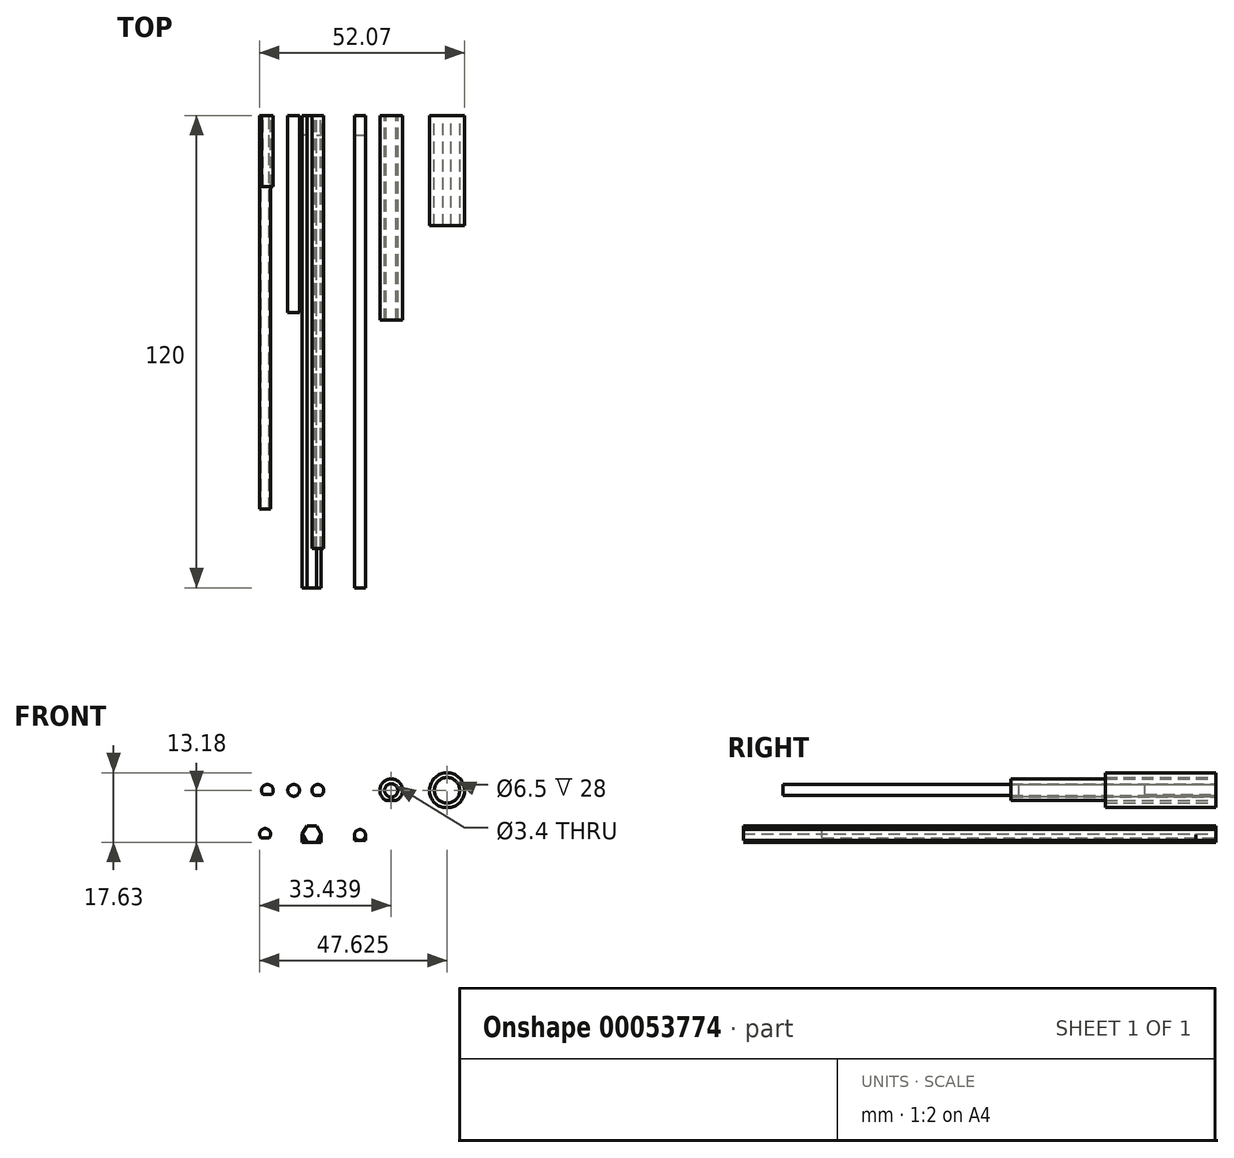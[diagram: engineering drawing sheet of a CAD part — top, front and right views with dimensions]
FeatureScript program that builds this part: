
annotation { "Feature Type Name" : "Feature", "Feature Type Description" : "" }
export const myFeature = defineFeature(function(context is Context, id is Id, definition is map)
    precondition{}
    {
        {
            var Q0;
            Q0=qCreatedBy(makeId("Front.planeOp"),FACE);
            var sketch = newSketch(context, id + "F0", { "sketchPlane" : qUnion([Q0])});
            skLineSegment(sketch, "E0", {"start": v(-14.5, 0) * mm, "end": v(47.28, 0) * mm, "construction": true});
            skLineSegment(sketch, "E1", {"start": v(-9.7, 3.28) * mm, "end": v(-9.7, -4.44) * mm, "construction": true});
            skCircle(sketch, "E2", {"center": v(-9.7, 0) * mm, "radius": 1.5 * mm});
            skPoint(sketch, "E3", {"position": v(-9.7, -1) * mm});
            skLineSegment(sketch, "E4", {"start": v(-10.82, -1) * mm, "end": v(-8.59, -1) * mm});
            skCircle(sketch, "E5", {"center": v(-3.04, 0) * mm, "radius": 1.5 * mm});
            skPoint(sketch, "E6", {"position": v(3.1, -1.3) * mm});
            skLineSegment(sketch, "E7", {"start": v(2.35, -1.3) * mm, "end": v(3.85, -1.3) * mm});
            skCircle(sketch, "E8", {"center": v(3.1, 0) * mm, "radius": 1.5 * mm});
            skLineSegment(sketch, "E9", {"start": v(7.92, -1.3) * mm, "end": v(9.42, -1.3) * mm});
            skCircle(sketch, "E10", {"center": v(8.67, 0) * mm, "radius": 1.5 * mm});
            skPoint(sketch, "E11", {"position": v(8.67, -1.3) * mm});
            skCircle(sketch, "E12", {"center": v(14.08, 0) * mm, "radius": 1.5 * mm});
            skLineSegment(sketch, "E13", {"start": v(13.33, -1.3) * mm, "end": v(14.83, -1.3) * mm});
            skPoint(sketch, "E14", {"position": v(14.08, -1.3) * mm});
            skCircle(sketch, "E15", {"center": v(21.75, 0) * mm, "radius": 1.7 * mm});
            skCircle(sketch, "E16", {"center": v(21.75, 0) * mm, "radius": 2.9 * mm});
            skLineSegment(sketch, "E17", {"start": v(21.75, 2.9) * mm, "end": v(21.75, -2.6) * mm, "construction": true});
            skLineSegment(sketch, "E18", {"start": v(20.46, -2.6) * mm, "end": v(23.03, -2.6) * mm});
            skCircle(sketch, "E19", {"center": v(-10.29, -11.1) * mm, "radius": 1.4 * mm});
            skLineSegment(sketch, "E20", {"start": v(-10.29, -7.78) * mm, "end": v(-10.29, -15.49) * mm, "construction": true});
            skLineSegment(sketch, "E21", {"start": v(-15.07, -11.1) * mm, "end": v(46.74, -11.1) * mm, "construction": true});
            skPoint(sketch, "E22", {"position": v(-10.29, -12.04) * mm});
            skLineSegment(sketch, "E23", {"start": v(-11.33, -12.04) * mm, "end": v(-9.25, -12.04) * mm});
            skCircle(sketch, "E24", {"center": v(35.93, 0) * mm, "radius": 4.45 * mm});
            skLineSegment(sketch, "E25", {"start": v(36.93, -4.34) * mm, "end": v(34.93, -4.34) * mm});
            skCircle(sketch, "E26", {"center": v(35.93, 0) * mm, "radius": 3.25 * mm});
            skCircle(sketch, "E27", {"center": v(1.53, -11.1) * mm, "radius": 2.4 * mm});
            skLineSegment(sketch, "E28.bottom", {"start": v(-0.87, -8.7) * mm, "end": v(3.93, -8.7) * mm});
            skLineSegment(sketch, "E28.top", {"start": v(-0.87, -13.18) * mm, "end": v(3.93, -13.18) * mm});
            skLineSegment(sketch, "E28.left", {"start": v(-0.87, -8.7) * mm, "end": v(-0.87, -13.18) * mm});
            skLineSegment(sketch, "E28.right", {"start": v(3.93, -8.7) * mm, "end": v(3.93, -13.18) * mm});
            skLineSegment(sketch, "E29", {"start": v(1.53, -8.7) * mm, "end": v(1.53, -13.5) * mm, "construction": true});
            skLineSegment(sketch, "E30.right", {"start": v(15.22, -9.95) * mm, "end": v(15.22, -12.75) * mm});
            skLineSegment(sketch, "E30.top", {"start": v(12.42, -12.75) * mm, "end": v(15.22, -12.75) * mm});
            skPoint(sketch, "E31", {"position": v(13.82, -11.35) * mm});
            skLineSegment(sketch, "E32", {"start": v(13.82, -9.95) * mm, "end": v(13.82, -12.75) * mm, "construction": true});
            skLineSegment(sketch, "E30.left", {"start": v(12.42, -9.95) * mm, "end": v(12.42, -12.75) * mm});
            skLineSegment(sketch, "E30.bottom", {"start": v(12.42, -9.95) * mm, "end": v(15.22, -9.95) * mm});
            skCircle(sketch, "E33", {"center": v(13.82, -11.35) * mm, "radius": 1.4 * mm});
            skPoint(sketch, "E34", {"position": v(0.33, -13.18) * mm});
            skPoint(sketch, "E35", {"position": v(2.73, -13.18) * mm});
            skCircle(sketch, "E36.cCircle", {"center": v(1.53, -11.1) * mm, "radius": 2.4 * mm, "construction": true});
            skLineSegment(sketch, "E36.0", {"start": v(-0.87, -11.1) * mm, "end": v(0.33, -9.03) * mm});
            skLineSegment(sketch, "E36.1", {"start": v(0.33, -9.03) * mm, "end": v(2.73, -9.03) * mm});
            skLineSegment(sketch, "E36.2", {"start": v(2.73, -9.03) * mm, "end": v(3.93, -11.1) * mm});
            skLineSegment(sketch, "E36.3", {"start": v(3.93, -11.1) * mm, "end": v(2.73, -13.18) * mm});
            skLineSegment(sketch, "E36.4", {"start": v(2.73, -13.18) * mm, "end": v(0.33, -13.18) * mm, "construction": true});
            skLineSegment(sketch, "E36.5", {"start": v(0.33, -13.18) * mm, "end": v(-0.87, -11.1) * mm});
            skSolve(sketch);
        }
        {
            var Q0;
            {var subQ0=sQuery(id+"F0.wireOp",EDGE,"E4");Q0=makeQuery(id+"F0.imprint","IMPRINT",FACE,{"disambiguationData":[TD([[makeQuery(id+"F0.imprint","IMPRINT",EDGE,{"derivedFrom":subQ0}),1.0]])]});}
            extrude(context, id + "F1", {"entities" : qUnion([Q0]), "depth" : 18 * mm});
        }
        {
            var Q0;
            Q0=makeQuery(id+"F0.imprint","IMPRINT",FACE,{"disambiguationData":[TD([[makeQuery(id+"F0.imprint","IMPRINT",EDGE,{"derivedFrom":sQuery(id+"F0.wireOp",EDGE,"E5")}),1.0]])]});
            extrude(context, id + "F2", {"entities" : qUnion([Q0]), "depth" : 50 * mm});
        }
        {
            var Q0;
            {var subQ0=sQuery(id+"F0.wireOp",EDGE,"E7");Q0=makeQuery(id+"F0.imprint","IMPRINT",FACE,{"disambiguationData":[TD([[makeQuery(id+"F0.imprint","IMPRINT",EDGE,{"derivedFrom":subQ0}),1.0]])]});}
            extrude(context, id + "F3", {"entities" : qUnion([Q0]), "depth" : 110 * mm});
        }
        {
            var Q0;
            {var subQ0=sQuery(id+"F0.wireOp",EDGE,"E23");Q0=makeQuery(id+"F0.imprint","IMPRINT",FACE,{"disambiguationData":[TD([[makeQuery(id+"F0.imprint","IMPRINT",EDGE,{"derivedFrom":subQ0}),1.0]])]});}
            extrude(context, id + "F4", {"entities" : qUnion([Q0]), "depth" : 100 * mm});
        }
        {
            var Q0;
            Q0=makeQuery(id+"F0.imprint","IMPRINT",FACE,{"disambiguationData":[TD([[makeQuery(id+"F0.imprint","IMPRINT",EDGE,{"derivedFrom":sQuery(id+"F0.wireOp",EDGE,"E15")}),-1.0]])]});
            extrude(context, id + "F5", {"entities" : qUnion([Q0]), "depth" : 52 * mm});
        }
        {
            var Q0;
            {var subQ0=sQuery(id+"F0.wireOp",EDGE,"E25");Q0=makeQuery(id+"F0.imprint","IMPRINT",FACE,{"disambiguationData":[TD([[makeQuery(id+"F0.imprint","IMPRINT",EDGE,{"derivedFrom":subQ0}),-1.0]])]});}
            extrude(context, id + "F6", {"entities" : qUnion([Q0]), "depth" : 28 * mm});
        }
        {
            var Q0;
            {var subQ0=sQuery(id+"F0.wireOp",EDGE,"E33");var subQ1=makeQuery(id+"F0.imprint","INTERSECT",VERTEX,{"derivedFrom":[sQuery(id+"F0.wireOp",EDGE,"E30.right"),subQ0]});Q0=makeQuery(id+"F0.imprint","IMPRINT",FACE,{"disambiguationData":[TD([[makeQuery(id+"F0.imprint","IMPRINT",EDGE,{"disambiguationData":[TD([[subQ1,-1.0]])],"derivedFrom":subQ0}),1.0]])]});}
            var Q1;
            {var subQ8=sQuery(id+"F0.wireOp",EDGE,"lmH1Ua7P-KBpo-EfuF-X9Tn-RCg2e1WFrg9c");Q1=makeQuery(id+"F0.imprint","IMPRINT",FACE,{"disambiguationData":[TD([[makeQuery(id+"F0.imprint","IMPRINT",EDGE,{"derivedFrom":subQ8}),1.0]])]});}
            var Q2;
            {var subQ0=sQuery(id+"F0.wireOp",EDGE,"sBpI47wx-J8by-lzRm-E1bE-YKL0DZhtYNUZ");Q2=makeQuery(id+"F0.imprint","IMPRINT",FACE,{"disambiguationData":[TD([[makeQuery(id+"F0.imprint","IMPRINT",EDGE,{"derivedFrom":subQ0}),-1.0]])]});}
            var Q3;
            {var subQ0=sQuery(id+"F0.wireOp",EDGE,"EQxFuaE4-UZCI-AMaP-Qjwn-iMiJtvs3Voor");Q3=makeQuery(id+"F0.imprint","IMPRINT",FACE,{"disambiguationData":[TD([[makeQuery(id+"F0.imprint","IMPRINT",EDGE,{"derivedFrom":subQ0}),1.0]])]});}
            var Q4;
            Q4=makeQuery(id+"F0.imprint","IMPRINT",FACE,{"disambiguationData":[TD([[makeQuery(id+"F0.imprint","IMPRINT",EDGE,{"derivedFrom":sQuery(id+"F0.wireOp",EDGE,"E36.0")}),-1.0]])]});
            extrude(context, id + "F7", {"entities" : qUnion([Q0, Q1, Q2, Q3, Q4]), "depth" : 120 * mm});
        }
        {
            var Q0;
            {var subQ0=sQuery(id+"F0.wireOp",EDGE,"EQxFuaE4-UZCI-AMaP-Qjwn-iMiJtvs3Voor");Q0=makeQuery(id+"F0.imprint","IMPRINT",FACE,{"disambiguationData":[TD([[makeQuery(id+"F0.imprint","IMPRINT",EDGE,{"derivedFrom":subQ0}),1.0]])]});}
            var Q1;
            {var subQ0=sQuery(id+"F0.wireOp",EDGE,"sBpI47wx-J8by-lzRm-E1bE-YKL0DZhtYNUZ");Q1=makeQuery(id+"F0.imprint","IMPRINT",FACE,{"disambiguationData":[TD([[makeQuery(id+"F0.imprint","IMPRINT",EDGE,{"derivedFrom":subQ0}),-1.0]])]});}
            var Q2;
            {var subQ1=sQuery(id+"F0.wireOp",EDGE,"E28.left");var subQ4=sQuery(id+"F0.wireOp",EDGE,"E28.top");var subQ6=makeQuery(id+"F0.imprint","INTERSECT",VERTEX,{"derivedFrom":[subQ4,subQ1]});Q2=makeQuery(id+"F0.imprint","IMPRINT",FACE,{"disambiguationData":[TD([[makeQuery(id+"F0.imprint","IMPRINT",EDGE,{"disambiguationData":[TD([[subQ6,-1.0]])],"derivedFrom":subQ4}),1.0]])]});}
            var Q3;
            {var subQ1=sQuery(id+"F0.wireOp",EDGE,"E28.right");var subQ4=sQuery(id+"F0.wireOp",EDGE,"E28.top");var subQ6=makeQuery(id+"F0.imprint","INTERSECT",VERTEX,{"derivedFrom":[subQ4,subQ1]});Q3=makeQuery(id+"F0.imprint","IMPRINT",FACE,{"disambiguationData":[TD([[makeQuery(id+"F0.imprint","IMPRINT",EDGE,{"disambiguationData":[TD([[subQ6,1.0]])],"derivedFrom":subQ4}),1.0]])]});}
            var Q4;
            {var subQ0=sQuery(id+"F0.wireOp",EDGE,"E36.3");Q4=makeQuery(id+"F0.imprint","IMPRINT",FACE,{"disambiguationData":[TD([[makeQuery(id+"F0.imprint","IMPRINT",EDGE,{"derivedFrom":subQ0}),1.0]])]});}
            var Q5;
            {var subQ0=sQuery(id+"F0.wireOp",EDGE,"E36.5");Q5=makeQuery(id+"F0.imprint","IMPRINT",FACE,{"disambiguationData":[TD([[makeQuery(id+"F0.imprint","IMPRINT",EDGE,{"derivedFrom":subQ0}),1.0]])]});}
            extrude(context, id + "F8", {"entities" : qUnion([Q0, Q1, Q2, Q3, Q4, Q5]), "operationType" : NewBodyOperationType.ADD, "depth" : 5 * mm});
        }
        {
            var Q0;
            {var subQ0=sQuery(id+"F0.wireOp",EDGE,"E30.left");var subQ1=sQuery(id+"F0.wireOp",EDGE,"E30.top");var subQ2=makeQuery(id+"F0.imprint","INTERSECT",VERTEX,{"derivedFrom":[subQ1,subQ0]});Q0=makeQuery(id+"F0.imprint","IMPRINT",FACE,{"disambiguationData":[TD([[makeQuery(id+"F0.imprint","IMPRINT",EDGE,{"disambiguationData":[TD([[subQ2,-1.0]])],"derivedFrom":subQ1}),1.0]])]});}
            var Q1;
            {var subQ0=sQuery(id+"F0.wireOp",EDGE,"E30.top");var subQ1=sQuery(id+"F0.wireOp",EDGE,"E30.right");var subQ2=makeQuery(id+"F0.imprint","INTERSECT",VERTEX,{"derivedFrom":[subQ1,subQ0]});Q1=makeQuery(id+"F0.imprint","IMPRINT",FACE,{"disambiguationData":[TD([[makeQuery(id+"F0.imprint","IMPRINT",EDGE,{"disambiguationData":[TD([[subQ2,1.0]])],"derivedFrom":subQ1}),-1.0]])]});}
            extrude(context, id + "F9", {"entities" : qUnion([Q0, Q1]), "operationType" : NewBodyOperationType.ADD, "depth" : 5 * mm});
        }
    });
